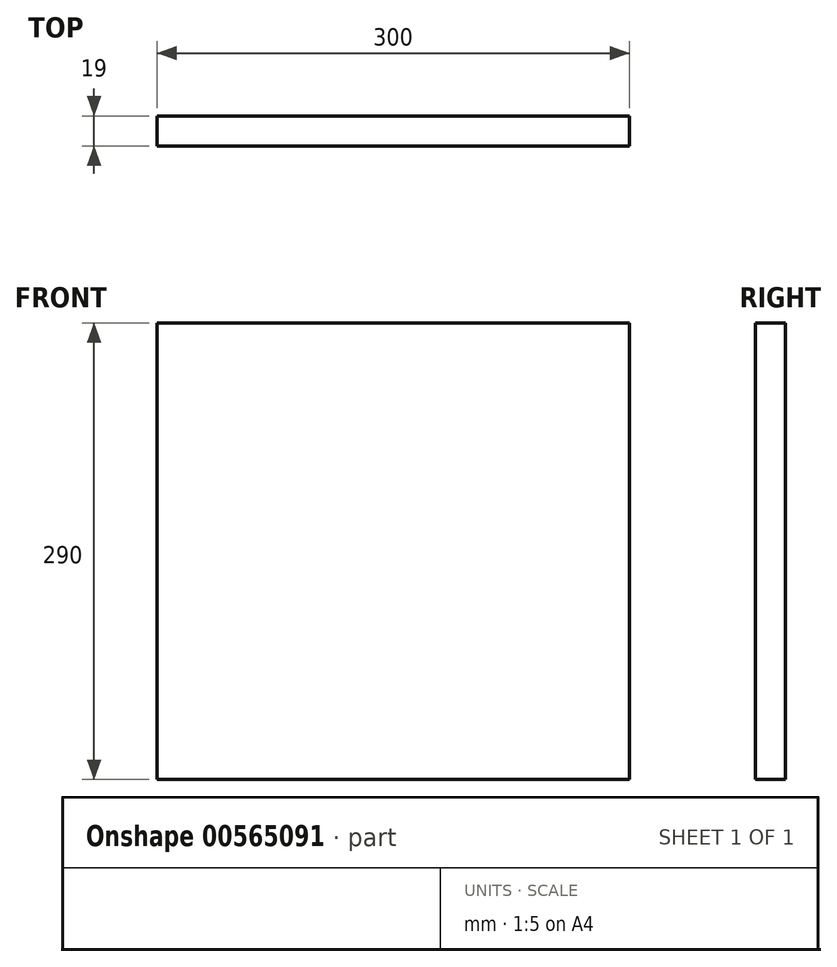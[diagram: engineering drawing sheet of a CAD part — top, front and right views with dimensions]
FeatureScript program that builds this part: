
annotation { "Feature Type Name" : "Feature", "Feature Type Description" : "" }
export const myFeature = defineFeature(function(context is Context, id is Id, definition is map)
    precondition{}
    {
        {
            var Q0;
            Q0=qCreatedBy(makeId("Front.planeOp"),FACE);
            var sketch = newSketch(context, id + "F0", { "sketchPlane" : qUnion([Q0])});
            skLineSegment(sketch, "E0.bottom", {"start": v(150, 145) * mm, "end": v(-150, 145) * mm});
            skLineSegment(sketch, "E0.top", {"start": v(150, -145) * mm, "end": v(-150, -145) * mm});
            skLineSegment(sketch, "E0.left", {"start": v(150, 145) * mm, "end": v(150, -145) * mm});
            skLineSegment(sketch, "E0.right", {"start": v(-150, 145) * mm, "end": v(-150, -145) * mm});
            skPoint(sketch, "E0.middle", {"position": v(0, 0) * mm});
            skSolve(sketch);
        }
        {
            var Q0;
            Q0=makeQuery(id+"F0.imprint","IMPRINT",FACE,{"disambiguationData":[TD([[makeQuery(id+"F0.imprint","IMPRINT",EDGE,{"derivedFrom":sQuery(id+"F0.wireOp",EDGE,"E0.bottom")}),1.0]])]});
            extrude(context, id + "F1", {"entities" : qUnion([Q0]), "depth" : 19 * mm, "offsetDistance" : 25 * mm});
        }
    });
